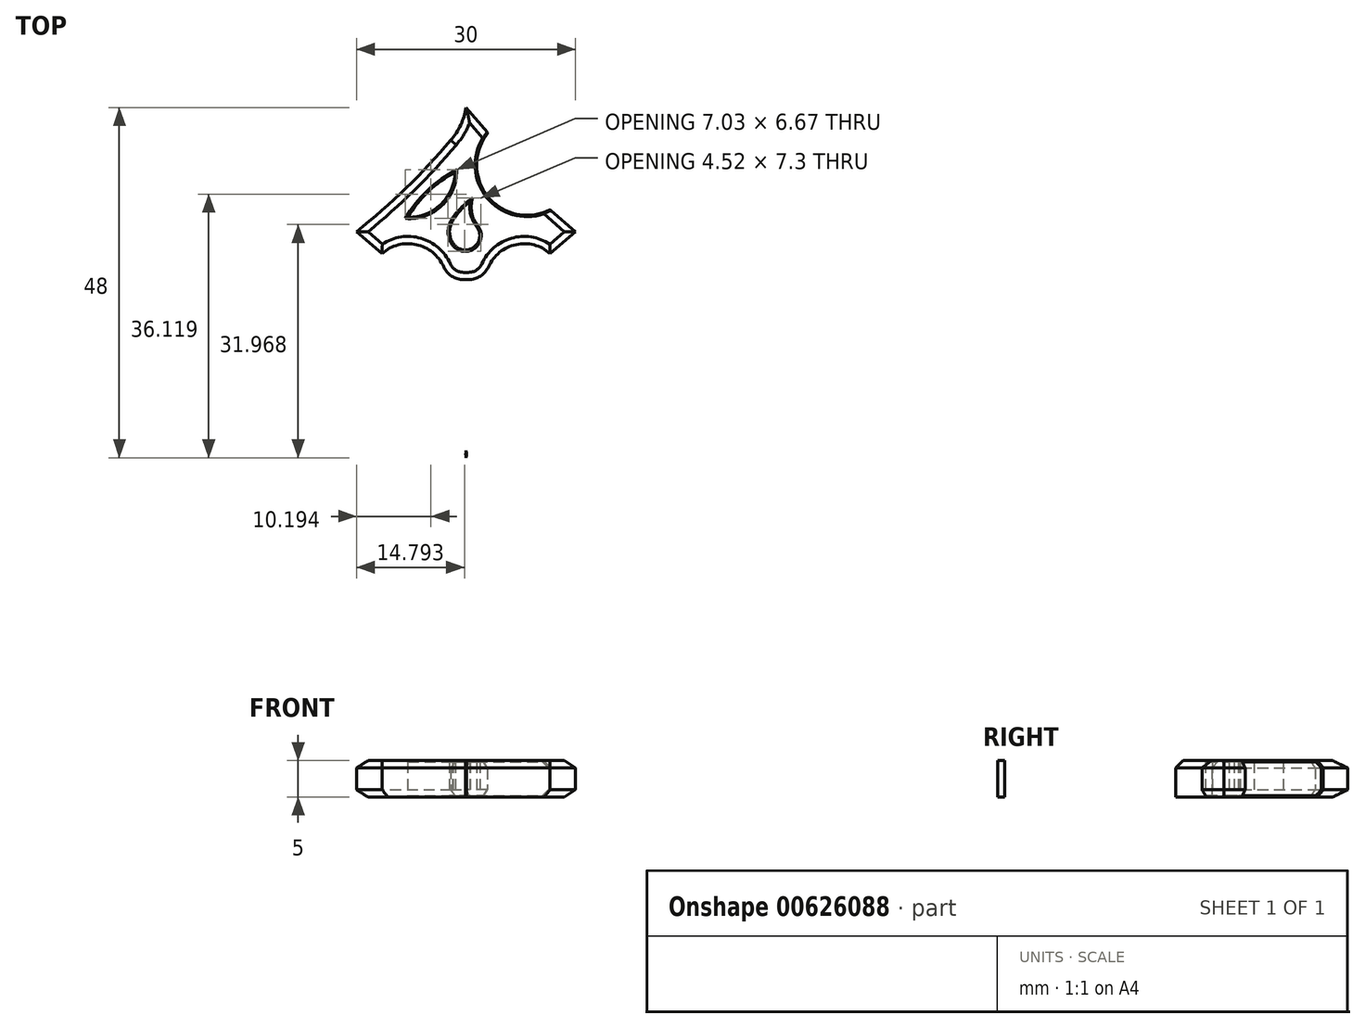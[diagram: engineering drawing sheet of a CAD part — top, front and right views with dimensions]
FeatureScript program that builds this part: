
annotation { "Feature Type Name" : "Feature", "Feature Type Description" : "" }
export const myFeature = defineFeature(function(context is Context, id is Id, definition is map)
    precondition{}
    {
        {
            var Q0;
            Q0=qCreatedBy(makeId("Top.planeOp"),FACE);
            var sketch = newSketch(context, id + "F0", { "sketchPlane" : qUnion([Q0])});
            skLineSegment(sketch, "E0", {"start": v(0, -20.9) * mm, "end": v(3, -20.9) * mm});
            skLineSegment(sketch, "E1", {"start": v(3, -20.9) * mm, "end": v(0, -20.9) * mm});
            skLineSegment(sketch, "E2", {"start": v(0, -20.9) * mm, "end": v(-3, -20.9) * mm});
            skLineSegment(sketch, "E3", {"start": v(-11.5, 6.6) * mm, "end": v(-11.5, 3.6) * mm});
            skLineSegment(sketch, "E4", {"start": v(11.5, 6.6) * mm, "end": v(11.5, 9.6) * mm});
            skLineSegment(sketch, "E5", {"start": v(11.5, 6.6) * mm, "end": v(11.5, 3.6) * mm});
            skLineSegment(sketch, "E6", {"start": v(0, 20.1) * mm, "end": v(3, 20.1) * mm});
            skLineSegment(sketch, "E7", {"start": v(0, 23.6) * mm, "end": v(3, 20.1) * mm});
            skLineSegment(sketch, "E8", {"start": v(15, 6.6) * mm, "end": v(11.5, 9.6) * mm});
            skLineSegment(sketch, "E9", {"start": v(15, 6.6) * mm, "end": v(11.5, 3.6) * mm});
            skLineSegment(sketch, "E10", {"start": v(0, -24.4) * mm, "end": v(3, -20.9) * mm});
            skLineSegment(sketch, "E11", {"start": v(0, -24.4) * mm, "end": v(-3, -20.9) * mm});
            skLineSegment(sketch, "E12", {"start": v(-11.5, 3.6) * mm, "end": v(-15, 6.6) * mm});
            skArc(sketch, "E13", {"start": v(-2.11, 19.11) * mm, "mid": v(-0.74, 21.2) * mm, "end": v(0, 23.6) * mm});
            skArc(sketch, "E14", {"start": v(-3, -20.9) * mm, "mid": v(-2.26, -10.46) * mm, "end": v(-2.62, 0) * mm});
            skArc(sketch, "E15", {"start": v(2.62, 0) * mm, "mid": v(2.26, -10.46) * mm, "end": v(3, -20.9) * mm});
            skArc(sketch, "E16", {"start": v(3, 20.1) * mm, "mid": v(2.98, 11.38) * mm, "end": v(11.5, 9.6) * mm});
            skLineSegment(sketch, "E17", {"start": v(-2.62, 0) * mm, "end": v(2.62, 0) * mm});
            skArc(sketch, "E18", {"start": v(-2.62, 0) * mm, "mid": v(-5.95, 4.54) * mm, "end": v(-11.5, 3.6) * mm});
            skArc(sketch, "E19", {"start": v(11.5, 3.6) * mm, "mid": v(5.95, 4.54) * mm, "end": v(2.62, 0) * mm});
            skArc(sketch, "E20", {"start": v(-7.98, 8.56) * mm, "mid": v(-3.46, 10.3) * mm, "end": v(-1.5, 14.72) * mm});
            skArc(sketch, "E21", {"start": v(-1.5, 14.72) * mm, "mid": v(-5.16, 12.08) * mm, "end": v(-7.98, 8.56) * mm});
            skArc(sketch, "E22", {"start": v(-15, 6.6) * mm, "mid": v(-8.24, 12.52) * mm, "end": v(-2.11, 19.11) * mm});
            skArc(sketch, "E23.0", {"start": v(-1.8, 5.01) * mm, "mid": v(1.02, 4.42) * mm, "end": v(1.45, 7.28) * mm});
            skArc(sketch, "E23.1", {"start": v(-1.88, 8.01) * mm, "mid": v(-2.27, 6.5) * mm, "end": v(-1.8, 5.01) * mm});
            skArc(sketch, "E24", {"start": v(0.58, 10.72) * mm, "mid": v(0.63, 8.9) * mm, "end": v(1.45, 7.28) * mm});
            skArc(sketch, "E25.trimOffspring", {"start": v(0.58, 10.72) * mm, "mid": v(-0.78, 9.48) * mm, "end": v(-1.88, 8.01) * mm});
            skSolve(sketch);
        }
        {
            var Q0;
            Q0=makeQuery(id+"F0.imprint","IMPRINT",FACE,{"disambiguationData":[TD([[makeQuery(id+"F0.imprint","IMPRINT",EDGE,{"derivedFrom":sQuery(id+"F0.wireOp",EDGE,"E1")}),-1.0]])]});
            var Q1;
            Q1=makeQuery(id+"F0.imprint","IMPRINT",FACE,{"disambiguationData":[TD([[makeQuery(id+"F0.imprint","IMPRINT",EDGE,{"derivedFrom":sQuery(id+"F0.wireOp",EDGE,"E1")}),1.0]])]});
            var Q2;
            Q2=makeQuery(id+"F0.imprint","IMPRINT",FACE,{"disambiguationData":[TD([[makeQuery(id+"F0.imprint","IMPRINT",EDGE,{"derivedFrom":sQuery(id+"F0.wireOp",EDGE,"E2")}),1.0]])]});
            var Q3;
            Q3=makeQuery(id+"F0.imprint","IMPRINT",FACE,{"disambiguationData":[TD([[makeQuery(id+"F0.imprint","IMPRINT",EDGE,{"derivedFrom":sQuery(id+"F0.wireOp",EDGE,"E4")}),-1.0]])]});
            var Q4;
            Q4=makeQuery(id+"F0.imprint","IMPRINT",FACE,{"disambiguationData":[TD([[makeQuery(id+"F0.imprint","IMPRINT",EDGE,{"derivedFrom":sQuery(id+"F0.wireOp",EDGE,"E4")}),1.0]])]});
            extrude(context, id + "F1", {"entities" : qUnion([Q0, Q1, Q2, Q3, Q4]), "depth" : 5 * mm, "offsetDistance" : 25 * mm});
        }
        {
            var Q0;
            Q0=makeQuery(id+"F1.opExtrude","SWEPT_EDGE",EDGE,{"disambiguationData":[OSD([sQuery(id+"F0.wireOp",EDGE,"k5tiwp8b-9EdK-JkDD-DdHM-JNxogL43b4vN"),sQuery(id+"F0.wireOp",EDGE,"E14")])]});
            var Q1;
            Q1=makeQuery(id+"F1.opExtrude","SWEPT_EDGE",EDGE,{"disambiguationData":[OSD([sQuery(id+"F0.wireOp",EDGE,"OUly3ajt-BEFw-R3yL-lqqk-aftP4KGx7Pbo"),sQuery(id+"F0.wireOp",EDGE,"E15")])]});
            var Q2;
            Q2=makeQuery(id+"F1.opExtrude","SWEPT_EDGE",EDGE,{"disambiguationData":[OSD([sQuery(id+"F0.wireOp",EDGE,"DrP2rqQ1-pYKq-EQtg-Zn2L-h3fUdfiGWgRb"),sQuery(id+"F0.wireOp",EDGE,"bePwl0fg-5cNm-J5ec-Xls5-XPhkgMzvfDfz")])]});
            fillet(context, id + "F2", {"entities" : qUnion([Q0, Q1, Q2]), "radius" : 3 * mm, "tangentPropagation" : true, "allowEdgeOverflow" : false});
        }
        {
            var Q0;
            Q0=makeQuery(id+"F1.opExtrude","CAP_EDGE",EDGE,{"disambiguationData":[OSD([sQuery(id+"F0.wireOp",EDGE,"hekDzvRY-LMJm-puWf-Dj4v-NQ24gZlVSRom")])],"isStart":false});
            var Q1;
            {var subQ0=sQuery(id+"F0.wireOp",EDGE,"hekDzvRY-LMJm-puWf-Dj4v-NQ24gZlVSRom");var subQ1=sQuery(id+"F0.wireOp",EDGE,"k5tiwp8b-9EdK-JkDD-DdHM-JNxogL43b4vN");Q1=makeQuery(id+"F2.opFillet","BLEND_EDGE",EDGE,{"blendedFrom":[makeQuery(id+"F1.opExtrude","SWEPT_EDGE",EDGE,{"disambiguationData":[OSD([subQ1,subQ0])]}),makeQuery(id+"F1.opExtrude","CAP_FACE",FACE,{"disambiguationData":[OSD([sQuery(id+"F0.wireOp",EDGE,"E7"),sQuery(id+"F0.wireOp",EDGE,"E8"),sQuery(id+"F0.wireOp",EDGE,"E9"),sQuery(id+"F0.wireOp",EDGE,"E10"),sQuery(id+"F0.wireOp",EDGE,"E11"),sQuery(id+"F0.wireOp",EDGE,"E12"),sQuery(id+"F0.wireOp",EDGE,"DrP2rqQ1-pYKq-EQtg-Zn2L-h3fUdfiGWgRb"),sQuery(id+"F0.wireOp",EDGE,"q6FidOOv-z0Xa-3gcV-Vxu2-K6z96FLS8LiD"),sQuery(id+"F0.wireOp",EDGE,"wHTpVqTk-c9Ss-kXag-DP7R-Z39pMIFVuknn"),sQuery(id+"F0.wireOp",EDGE,"bePwl0fg-5cNm-J5ec-Xls5-XPhkgMzvfDfz"),sQuery(id+"F0.wireOp",EDGE,"OUly3ajt-BEFw-R3yL-lqqk-aftP4KGx7Pbo"),subQ1,subQ0,sQuery(id+"F0.wireOp",EDGE,"mn51xUnX-rDYS-26zJ-xgYu-js4L2MmEVdlG"),sQuery(id+"F0.wireOp",EDGE,"lCkpgf7s-SHDd-Mj0l-YXK1-aCLSxgwuS06x"),sQuery(id+"F0.wireOp",EDGE,"lZJrJr9u-5WJ1-CQOP-RMIl-6jj2P56iwayc"),sQuery(id+"F0.wireOp",EDGE,"E13"),sQuery(id+"F0.wireOp",EDGE,"1a699431-0b08-407c-8c22-9d53338cef66.0"),sQuery(id+"F0.wireOp",EDGE,"1a699431-0b08-407c-8c22-9d53338cef66.1"),sQuery(id+"F0.wireOp",EDGE,"1a699431-0b08-407c-8c22-9d53338cef66.2"),sQuery(id+"F0.wireOp",EDGE,"1a699431-0b08-407c-8c22-9d53338cef66.3"),sQuery(id+"F0.wireOp",EDGE,"1a699431-0b08-407c-8c22-9d53338cef66.4"),sQuery(id+"F0.wireOp",EDGE,"1a699431-0b08-407c-8c22-9d53338cef66.5")])],"isStart":false})],"blendedInto":[makeQuery(id+"F1.opExtrude","CAP_FACE",FACE,{"disambiguationData":[OSD([sQuery(id+"F0.wireOp",EDGE,"E7"),sQuery(id+"F0.wireOp",EDGE,"E8"),sQuery(id+"F0.wireOp",EDGE,"E9"),sQuery(id+"F0.wireOp",EDGE,"E10"),sQuery(id+"F0.wireOp",EDGE,"E11"),sQuery(id+"F0.wireOp",EDGE,"E12"),sQuery(id+"F0.wireOp",EDGE,"DrP2rqQ1-pYKq-EQtg-Zn2L-h3fUdfiGWgRb"),sQuery(id+"F0.wireOp",EDGE,"q6FidOOv-z0Xa-3gcV-Vxu2-K6z96FLS8LiD"),sQuery(id+"F0.wireOp",EDGE,"wHTpVqTk-c9Ss-kXag-DP7R-Z39pMIFVuknn"),sQuery(id+"F0.wireOp",EDGE,"bePwl0fg-5cNm-J5ec-Xls5-XPhkgMzvfDfz"),sQuery(id+"F0.wireOp",EDGE,"OUly3ajt-BEFw-R3yL-lqqk-aftP4KGx7Pbo"),subQ1,subQ0,sQuery(id+"F0.wireOp",EDGE,"mn51xUnX-rDYS-26zJ-xgYu-js4L2MmEVdlG"),sQuery(id+"F0.wireOp",EDGE,"lCkpgf7s-SHDd-Mj0l-YXK1-aCLSxgwuS06x"),sQuery(id+"F0.wireOp",EDGE,"lZJrJr9u-5WJ1-CQOP-RMIl-6jj2P56iwayc"),sQuery(id+"F0.wireOp",EDGE,"E13"),sQuery(id+"F0.wireOp",EDGE,"1a699431-0b08-407c-8c22-9d53338cef66.0"),sQuery(id+"F0.wireOp",EDGE,"1a699431-0b08-407c-8c22-9d53338cef66.1"),sQuery(id+"F0.wireOp",EDGE,"1a699431-0b08-407c-8c22-9d53338cef66.2"),sQuery(id+"F0.wireOp",EDGE,"1a699431-0b08-407c-8c22-9d53338cef66.3"),sQuery(id+"F0.wireOp",EDGE,"1a699431-0b08-407c-8c22-9d53338cef66.4"),sQuery(id+"F0.wireOp",EDGE,"1a699431-0b08-407c-8c22-9d53338cef66.5")])],"isStart":false})]});}
            var Q2;
            Q2=makeQuery(id+"F1.opExtrude","CAP_EDGE",EDGE,{"disambiguationData":[OSD([sQuery(id+"F0.wireOp",EDGE,"k5tiwp8b-9EdK-JkDD-DdHM-JNxogL43b4vN")])],"isStart":false});
            var Q3;
            Q3=makeQuery(id+"F1.opExtrude","CAP_EDGE",EDGE,{"disambiguationData":[OSD([sQuery(id+"F0.wireOp",EDGE,"E12")])],"isStart":false});
            var Q4;
            Q4=makeQuery(id+"F1.opExtrude","CAP_EDGE",EDGE,{"disambiguationData":[OSD([sQuery(id+"F0.wireOp",EDGE,"lZJrJr9u-5WJ1-CQOP-RMIl-6jj2P56iwayc")])],"isStart":false});
            var Q5;
            Q5=makeQuery(id+"F1.opExtrude","CAP_EDGE",EDGE,{"disambiguationData":[OSD([sQuery(id+"F0.wireOp",EDGE,"E13")])],"isStart":false});
            var Q6;
            Q6=makeQuery(id+"F1.opExtrude","CAP_EDGE",EDGE,{"disambiguationData":[OSD([sQuery(id+"F0.wireOp",EDGE,"E7")])],"isStart":false});
            var Q7;
            Q7=makeQuery(id+"F1.opExtrude","CAP_EDGE",EDGE,{"disambiguationData":[OSD([sQuery(id+"F0.wireOp",EDGE,"DrP2rqQ1-pYKq-EQtg-Zn2L-h3fUdfiGWgRb")])],"isStart":false});
            var Q8;
            {var subQ0=sQuery(id+"F0.wireOp",EDGE,"bePwl0fg-5cNm-J5ec-Xls5-XPhkgMzvfDfz");var subQ1=sQuery(id+"F0.wireOp",EDGE,"DrP2rqQ1-pYKq-EQtg-Zn2L-h3fUdfiGWgRb");Q8=makeQuery(id+"F2.opFillet","BLEND_EDGE",EDGE,{"blendedFrom":[makeQuery(id+"F1.opExtrude","SWEPT_EDGE",EDGE,{"disambiguationData":[OSD([subQ1,subQ0])]}),makeQuery(id+"F1.opExtrude","CAP_FACE",FACE,{"disambiguationData":[OSD([sQuery(id+"F0.wireOp",EDGE,"E7"),sQuery(id+"F0.wireOp",EDGE,"E8"),sQuery(id+"F0.wireOp",EDGE,"E9"),sQuery(id+"F0.wireOp",EDGE,"E10"),sQuery(id+"F0.wireOp",EDGE,"E11"),sQuery(id+"F0.wireOp",EDGE,"E12"),subQ1,sQuery(id+"F0.wireOp",EDGE,"q6FidOOv-z0Xa-3gcV-Vxu2-K6z96FLS8LiD"),sQuery(id+"F0.wireOp",EDGE,"wHTpVqTk-c9Ss-kXag-DP7R-Z39pMIFVuknn"),subQ0,sQuery(id+"F0.wireOp",EDGE,"OUly3ajt-BEFw-R3yL-lqqk-aftP4KGx7Pbo"),sQuery(id+"F0.wireOp",EDGE,"k5tiwp8b-9EdK-JkDD-DdHM-JNxogL43b4vN"),sQuery(id+"F0.wireOp",EDGE,"hekDzvRY-LMJm-puWf-Dj4v-NQ24gZlVSRom"),sQuery(id+"F0.wireOp",EDGE,"mn51xUnX-rDYS-26zJ-xgYu-js4L2MmEVdlG"),sQuery(id+"F0.wireOp",EDGE,"lCkpgf7s-SHDd-Mj0l-YXK1-aCLSxgwuS06x"),sQuery(id+"F0.wireOp",EDGE,"lZJrJr9u-5WJ1-CQOP-RMIl-6jj2P56iwayc"),sQuery(id+"F0.wireOp",EDGE,"E13"),sQuery(id+"F0.wireOp",EDGE,"1a699431-0b08-407c-8c22-9d53338cef66.0"),sQuery(id+"F0.wireOp",EDGE,"1a699431-0b08-407c-8c22-9d53338cef66.1"),sQuery(id+"F0.wireOp",EDGE,"1a699431-0b08-407c-8c22-9d53338cef66.2"),sQuery(id+"F0.wireOp",EDGE,"1a699431-0b08-407c-8c22-9d53338cef66.3"),sQuery(id+"F0.wireOp",EDGE,"1a699431-0b08-407c-8c22-9d53338cef66.4"),sQuery(id+"F0.wireOp",EDGE,"1a699431-0b08-407c-8c22-9d53338cef66.5")])],"isStart":false})],"blendedInto":[makeQuery(id+"F1.opExtrude","CAP_FACE",FACE,{"disambiguationData":[OSD([sQuery(id+"F0.wireOp",EDGE,"E7"),sQuery(id+"F0.wireOp",EDGE,"E8"),sQuery(id+"F0.wireOp",EDGE,"E9"),sQuery(id+"F0.wireOp",EDGE,"E10"),sQuery(id+"F0.wireOp",EDGE,"E11"),sQuery(id+"F0.wireOp",EDGE,"E12"),subQ1,sQuery(id+"F0.wireOp",EDGE,"q6FidOOv-z0Xa-3gcV-Vxu2-K6z96FLS8LiD"),sQuery(id+"F0.wireOp",EDGE,"wHTpVqTk-c9Ss-kXag-DP7R-Z39pMIFVuknn"),subQ0,sQuery(id+"F0.wireOp",EDGE,"OUly3ajt-BEFw-R3yL-lqqk-aftP4KGx7Pbo"),sQuery(id+"F0.wireOp",EDGE,"k5tiwp8b-9EdK-JkDD-DdHM-JNxogL43b4vN"),sQuery(id+"F0.wireOp",EDGE,"hekDzvRY-LMJm-puWf-Dj4v-NQ24gZlVSRom"),sQuery(id+"F0.wireOp",EDGE,"mn51xUnX-rDYS-26zJ-xgYu-js4L2MmEVdlG"),sQuery(id+"F0.wireOp",EDGE,"lCkpgf7s-SHDd-Mj0l-YXK1-aCLSxgwuS06x"),sQuery(id+"F0.wireOp",EDGE,"lZJrJr9u-5WJ1-CQOP-RMIl-6jj2P56iwayc"),sQuery(id+"F0.wireOp",EDGE,"E13"),sQuery(id+"F0.wireOp",EDGE,"1a699431-0b08-407c-8c22-9d53338cef66.0"),sQuery(id+"F0.wireOp",EDGE,"1a699431-0b08-407c-8c22-9d53338cef66.1"),sQuery(id+"F0.wireOp",EDGE,"1a699431-0b08-407c-8c22-9d53338cef66.2"),sQuery(id+"F0.wireOp",EDGE,"1a699431-0b08-407c-8c22-9d53338cef66.3"),sQuery(id+"F0.wireOp",EDGE,"1a699431-0b08-407c-8c22-9d53338cef66.4"),sQuery(id+"F0.wireOp",EDGE,"1a699431-0b08-407c-8c22-9d53338cef66.5")])],"isStart":false})]});}
            var Q9;
            Q9=makeQuery(id+"F1.opExtrude","CAP_EDGE",EDGE,{"disambiguationData":[OSD([sQuery(id+"F0.wireOp",EDGE,"bePwl0fg-5cNm-J5ec-Xls5-XPhkgMzvfDfz")])],"isStart":false});
            var Q10;
            Q10=makeQuery(id+"F1.opExtrude","CAP_EDGE",EDGE,{"disambiguationData":[OSD([sQuery(id+"F0.wireOp",EDGE,"E8")])],"isStart":false});
            var Q11;
            Q11=makeQuery(id+"F1.opExtrude","CAP_EDGE",EDGE,{"disambiguationData":[OSD([sQuery(id+"F0.wireOp",EDGE,"E9")])],"isStart":false});
            var Q12;
            Q12=makeQuery(id+"F1.opExtrude","CAP_EDGE",EDGE,{"disambiguationData":[OSD([sQuery(id+"F0.wireOp",EDGE,"OUly3ajt-BEFw-R3yL-lqqk-aftP4KGx7Pbo")])],"isStart":false});
            var Q13;
            {var subQ0=sQuery(id+"F0.wireOp",EDGE,"mn51xUnX-rDYS-26zJ-xgYu-js4L2MmEVdlG");var subQ1=sQuery(id+"F0.wireOp",EDGE,"OUly3ajt-BEFw-R3yL-lqqk-aftP4KGx7Pbo");Q13=makeQuery(id+"F2.opFillet","BLEND_EDGE",EDGE,{"blendedFrom":[makeQuery(id+"F1.opExtrude","SWEPT_EDGE",EDGE,{"disambiguationData":[OSD([subQ1,subQ0])]}),makeQuery(id+"F1.opExtrude","CAP_FACE",FACE,{"disambiguationData":[OSD([sQuery(id+"F0.wireOp",EDGE,"E7"),sQuery(id+"F0.wireOp",EDGE,"E8"),sQuery(id+"F0.wireOp",EDGE,"E9"),sQuery(id+"F0.wireOp",EDGE,"E10"),sQuery(id+"F0.wireOp",EDGE,"E11"),sQuery(id+"F0.wireOp",EDGE,"E12"),sQuery(id+"F0.wireOp",EDGE,"DrP2rqQ1-pYKq-EQtg-Zn2L-h3fUdfiGWgRb"),sQuery(id+"F0.wireOp",EDGE,"q6FidOOv-z0Xa-3gcV-Vxu2-K6z96FLS8LiD"),sQuery(id+"F0.wireOp",EDGE,"wHTpVqTk-c9Ss-kXag-DP7R-Z39pMIFVuknn"),sQuery(id+"F0.wireOp",EDGE,"bePwl0fg-5cNm-J5ec-Xls5-XPhkgMzvfDfz"),subQ1,sQuery(id+"F0.wireOp",EDGE,"k5tiwp8b-9EdK-JkDD-DdHM-JNxogL43b4vN"),sQuery(id+"F0.wireOp",EDGE,"hekDzvRY-LMJm-puWf-Dj4v-NQ24gZlVSRom"),subQ0,sQuery(id+"F0.wireOp",EDGE,"lCkpgf7s-SHDd-Mj0l-YXK1-aCLSxgwuS06x"),sQuery(id+"F0.wireOp",EDGE,"lZJrJr9u-5WJ1-CQOP-RMIl-6jj2P56iwayc"),sQuery(id+"F0.wireOp",EDGE,"E13"),sQuery(id+"F0.wireOp",EDGE,"1a699431-0b08-407c-8c22-9d53338cef66.0"),sQuery(id+"F0.wireOp",EDGE,"1a699431-0b08-407c-8c22-9d53338cef66.1"),sQuery(id+"F0.wireOp",EDGE,"1a699431-0b08-407c-8c22-9d53338cef66.2"),sQuery(id+"F0.wireOp",EDGE,"1a699431-0b08-407c-8c22-9d53338cef66.3"),sQuery(id+"F0.wireOp",EDGE,"1a699431-0b08-407c-8c22-9d53338cef66.4"),sQuery(id+"F0.wireOp",EDGE,"1a699431-0b08-407c-8c22-9d53338cef66.5")])],"isStart":false})],"blendedInto":[makeQuery(id+"F1.opExtrude","CAP_FACE",FACE,{"disambiguationData":[OSD([sQuery(id+"F0.wireOp",EDGE,"E7"),sQuery(id+"F0.wireOp",EDGE,"E8"),sQuery(id+"F0.wireOp",EDGE,"E9"),sQuery(id+"F0.wireOp",EDGE,"E10"),sQuery(id+"F0.wireOp",EDGE,"E11"),sQuery(id+"F0.wireOp",EDGE,"E12"),sQuery(id+"F0.wireOp",EDGE,"DrP2rqQ1-pYKq-EQtg-Zn2L-h3fUdfiGWgRb"),sQuery(id+"F0.wireOp",EDGE,"q6FidOOv-z0Xa-3gcV-Vxu2-K6z96FLS8LiD"),sQuery(id+"F0.wireOp",EDGE,"wHTpVqTk-c9Ss-kXag-DP7R-Z39pMIFVuknn"),sQuery(id+"F0.wireOp",EDGE,"bePwl0fg-5cNm-J5ec-Xls5-XPhkgMzvfDfz"),subQ1,sQuery(id+"F0.wireOp",EDGE,"k5tiwp8b-9EdK-JkDD-DdHM-JNxogL43b4vN"),sQuery(id+"F0.wireOp",EDGE,"hekDzvRY-LMJm-puWf-Dj4v-NQ24gZlVSRom"),subQ0,sQuery(id+"F0.wireOp",EDGE,"lCkpgf7s-SHDd-Mj0l-YXK1-aCLSxgwuS06x"),sQuery(id+"F0.wireOp",EDGE,"lZJrJr9u-5WJ1-CQOP-RMIl-6jj2P56iwayc"),sQuery(id+"F0.wireOp",EDGE,"E13"),sQuery(id+"F0.wireOp",EDGE,"1a699431-0b08-407c-8c22-9d53338cef66.0"),sQuery(id+"F0.wireOp",EDGE,"1a699431-0b08-407c-8c22-9d53338cef66.1"),sQuery(id+"F0.wireOp",EDGE,"1a699431-0b08-407c-8c22-9d53338cef66.2"),sQuery(id+"F0.wireOp",EDGE,"1a699431-0b08-407c-8c22-9d53338cef66.3"),sQuery(id+"F0.wireOp",EDGE,"1a699431-0b08-407c-8c22-9d53338cef66.4"),sQuery(id+"F0.wireOp",EDGE,"1a699431-0b08-407c-8c22-9d53338cef66.5")])],"isStart":false})]});}
            var Q14;
            Q14=makeQuery(id+"F1.opExtrude","CAP_EDGE",EDGE,{"disambiguationData":[OSD([sQuery(id+"F0.wireOp",EDGE,"mn51xUnX-rDYS-26zJ-xgYu-js4L2MmEVdlG")])],"isStart":false});
            var Q15;
            Q15=makeQuery(id+"F1.opExtrude","CAP_EDGE",EDGE,{"disambiguationData":[OSD([sQuery(id+"F0.wireOp",EDGE,"k5tiwp8b-9EdK-JkDD-DdHM-JNxogL43b4vN")])],"isStart":true});
            var Q16;
            Q16=makeQuery(id+"F1.opExtrude","CAP_EDGE",EDGE,{"disambiguationData":[OSD([sQuery(id+"F0.wireOp",EDGE,"E12")])],"isStart":true});
            var Q17;
            Q17=makeQuery(id+"F1.opExtrude","CAP_EDGE",EDGE,{"disambiguationData":[OSD([sQuery(id+"F0.wireOp",EDGE,"OUly3ajt-BEFw-R3yL-lqqk-aftP4KGx7Pbo")])],"isStart":true});
            var Q18;
            Q18=makeQuery(id+"F1.opExtrude","CAP_EDGE",EDGE,{"disambiguationData":[OSD([sQuery(id+"F0.wireOp",EDGE,"bePwl0fg-5cNm-J5ec-Xls5-XPhkgMzvfDfz")])],"isStart":true});
            var Q19;
            Q19=makeQuery(id+"F1.opExtrude","CAP_EDGE",EDGE,{"disambiguationData":[OSD([sQuery(id+"F0.wireOp",EDGE,"lZJrJr9u-5WJ1-CQOP-RMIl-6jj2P56iwayc")])],"isStart":true});
            var Q20;
            {var subQ0=sQuery(id+"F0.wireOp",EDGE,"hekDzvRY-LMJm-puWf-Dj4v-NQ24gZlVSRom");var subQ1=sQuery(id+"F0.wireOp",EDGE,"k5tiwp8b-9EdK-JkDD-DdHM-JNxogL43b4vN");Q20=makeQuery(id+"F2.opFillet","BLEND_EDGE",EDGE,{"blendedFrom":[makeQuery(id+"F1.opExtrude","SWEPT_EDGE",EDGE,{"disambiguationData":[OSD([subQ1,subQ0])]}),makeQuery(id+"F1.opExtrude","CAP_FACE",FACE,{"disambiguationData":[OSD([sQuery(id+"F0.wireOp",EDGE,"E7"),sQuery(id+"F0.wireOp",EDGE,"E8"),sQuery(id+"F0.wireOp",EDGE,"E9"),sQuery(id+"F0.wireOp",EDGE,"E10"),sQuery(id+"F0.wireOp",EDGE,"E11"),sQuery(id+"F0.wireOp",EDGE,"E12"),sQuery(id+"F0.wireOp",EDGE,"DrP2rqQ1-pYKq-EQtg-Zn2L-h3fUdfiGWgRb"),sQuery(id+"F0.wireOp",EDGE,"q6FidOOv-z0Xa-3gcV-Vxu2-K6z96FLS8LiD"),sQuery(id+"F0.wireOp",EDGE,"wHTpVqTk-c9Ss-kXag-DP7R-Z39pMIFVuknn"),sQuery(id+"F0.wireOp",EDGE,"bePwl0fg-5cNm-J5ec-Xls5-XPhkgMzvfDfz"),sQuery(id+"F0.wireOp",EDGE,"OUly3ajt-BEFw-R3yL-lqqk-aftP4KGx7Pbo"),subQ1,subQ0,sQuery(id+"F0.wireOp",EDGE,"mn51xUnX-rDYS-26zJ-xgYu-js4L2MmEVdlG"),sQuery(id+"F0.wireOp",EDGE,"lCkpgf7s-SHDd-Mj0l-YXK1-aCLSxgwuS06x"),sQuery(id+"F0.wireOp",EDGE,"lZJrJr9u-5WJ1-CQOP-RMIl-6jj2P56iwayc"),sQuery(id+"F0.wireOp",EDGE,"E13"),sQuery(id+"F0.wireOp",EDGE,"1a699431-0b08-407c-8c22-9d53338cef66.0"),sQuery(id+"F0.wireOp",EDGE,"1a699431-0b08-407c-8c22-9d53338cef66.1"),sQuery(id+"F0.wireOp",EDGE,"1a699431-0b08-407c-8c22-9d53338cef66.2"),sQuery(id+"F0.wireOp",EDGE,"1a699431-0b08-407c-8c22-9d53338cef66.3"),sQuery(id+"F0.wireOp",EDGE,"1a699431-0b08-407c-8c22-9d53338cef66.4"),sQuery(id+"F0.wireOp",EDGE,"1a699431-0b08-407c-8c22-9d53338cef66.5")])],"isStart":true})],"blendedInto":[makeQuery(id+"F1.opExtrude","CAP_FACE",FACE,{"disambiguationData":[OSD([sQuery(id+"F0.wireOp",EDGE,"E7"),sQuery(id+"F0.wireOp",EDGE,"E8"),sQuery(id+"F0.wireOp",EDGE,"E9"),sQuery(id+"F0.wireOp",EDGE,"E10"),sQuery(id+"F0.wireOp",EDGE,"E11"),sQuery(id+"F0.wireOp",EDGE,"E12"),sQuery(id+"F0.wireOp",EDGE,"DrP2rqQ1-pYKq-EQtg-Zn2L-h3fUdfiGWgRb"),sQuery(id+"F0.wireOp",EDGE,"q6FidOOv-z0Xa-3gcV-Vxu2-K6z96FLS8LiD"),sQuery(id+"F0.wireOp",EDGE,"wHTpVqTk-c9Ss-kXag-DP7R-Z39pMIFVuknn"),sQuery(id+"F0.wireOp",EDGE,"bePwl0fg-5cNm-J5ec-Xls5-XPhkgMzvfDfz"),sQuery(id+"F0.wireOp",EDGE,"OUly3ajt-BEFw-R3yL-lqqk-aftP4KGx7Pbo"),subQ1,subQ0,sQuery(id+"F0.wireOp",EDGE,"mn51xUnX-rDYS-26zJ-xgYu-js4L2MmEVdlG"),sQuery(id+"F0.wireOp",EDGE,"lCkpgf7s-SHDd-Mj0l-YXK1-aCLSxgwuS06x"),sQuery(id+"F0.wireOp",EDGE,"lZJrJr9u-5WJ1-CQOP-RMIl-6jj2P56iwayc"),sQuery(id+"F0.wireOp",EDGE,"E13"),sQuery(id+"F0.wireOp",EDGE,"1a699431-0b08-407c-8c22-9d53338cef66.0"),sQuery(id+"F0.wireOp",EDGE,"1a699431-0b08-407c-8c22-9d53338cef66.1"),sQuery(id+"F0.wireOp",EDGE,"1a699431-0b08-407c-8c22-9d53338cef66.2"),sQuery(id+"F0.wireOp",EDGE,"1a699431-0b08-407c-8c22-9d53338cef66.3"),sQuery(id+"F0.wireOp",EDGE,"1a699431-0b08-407c-8c22-9d53338cef66.4"),sQuery(id+"F0.wireOp",EDGE,"1a699431-0b08-407c-8c22-9d53338cef66.5")])],"isStart":true})]});}
            var Q21;
            Q21=makeQuery(id+"F1.opExtrude","CAP_EDGE",EDGE,{"disambiguationData":[OSD([sQuery(id+"F0.wireOp",EDGE,"hekDzvRY-LMJm-puWf-Dj4v-NQ24gZlVSRom")])],"isStart":true});
            var Q22;
            Q22=makeQuery(id+"F1.opExtrude","CAP_EDGE",EDGE,{"disambiguationData":[OSD([sQuery(id+"F0.wireOp",EDGE,"E11")])],"isStart":false});
            var Q23;
            Q23=makeQuery(id+"F1.opExtrude","CAP_EDGE",EDGE,{"disambiguationData":[OSD([sQuery(id+"F0.wireOp",EDGE,"E10")])],"isStart":false});
            var Q24;
            Q24=makeQuery(id+"F1.opExtrude","CAP_EDGE",EDGE,{"disambiguationData":[OSD([sQuery(id+"F0.wireOp",EDGE,"E11")])],"isStart":true});
            var Q25;
            Q25=makeQuery(id+"F1.opExtrude","CAP_EDGE",EDGE,{"disambiguationData":[OSD([sQuery(id+"F0.wireOp",EDGE,"E10")])],"isStart":true});
            var Q26;
            Q26=makeQuery(id+"F1.opExtrude","CAP_EDGE",EDGE,{"disambiguationData":[OSD([sQuery(id+"F0.wireOp",EDGE,"mn51xUnX-rDYS-26zJ-xgYu-js4L2MmEVdlG")])],"isStart":true});
            var Q27;
            {var subQ0=sQuery(id+"F0.wireOp",EDGE,"mn51xUnX-rDYS-26zJ-xgYu-js4L2MmEVdlG");var subQ1=sQuery(id+"F0.wireOp",EDGE,"OUly3ajt-BEFw-R3yL-lqqk-aftP4KGx7Pbo");Q27=makeQuery(id+"F2.opFillet","BLEND_EDGE",EDGE,{"blendedFrom":[makeQuery(id+"F1.opExtrude","SWEPT_EDGE",EDGE,{"disambiguationData":[OSD([subQ1,subQ0])]}),makeQuery(id+"F1.opExtrude","CAP_FACE",FACE,{"disambiguationData":[OSD([sQuery(id+"F0.wireOp",EDGE,"E7"),sQuery(id+"F0.wireOp",EDGE,"E8"),sQuery(id+"F0.wireOp",EDGE,"E9"),sQuery(id+"F0.wireOp",EDGE,"E10"),sQuery(id+"F0.wireOp",EDGE,"E11"),sQuery(id+"F0.wireOp",EDGE,"E12"),sQuery(id+"F0.wireOp",EDGE,"DrP2rqQ1-pYKq-EQtg-Zn2L-h3fUdfiGWgRb"),sQuery(id+"F0.wireOp",EDGE,"q6FidOOv-z0Xa-3gcV-Vxu2-K6z96FLS8LiD"),sQuery(id+"F0.wireOp",EDGE,"wHTpVqTk-c9Ss-kXag-DP7R-Z39pMIFVuknn"),sQuery(id+"F0.wireOp",EDGE,"bePwl0fg-5cNm-J5ec-Xls5-XPhkgMzvfDfz"),subQ1,sQuery(id+"F0.wireOp",EDGE,"k5tiwp8b-9EdK-JkDD-DdHM-JNxogL43b4vN"),sQuery(id+"F0.wireOp",EDGE,"hekDzvRY-LMJm-puWf-Dj4v-NQ24gZlVSRom"),subQ0,sQuery(id+"F0.wireOp",EDGE,"lCkpgf7s-SHDd-Mj0l-YXK1-aCLSxgwuS06x"),sQuery(id+"F0.wireOp",EDGE,"lZJrJr9u-5WJ1-CQOP-RMIl-6jj2P56iwayc"),sQuery(id+"F0.wireOp",EDGE,"E13"),sQuery(id+"F0.wireOp",EDGE,"1a699431-0b08-407c-8c22-9d53338cef66.0"),sQuery(id+"F0.wireOp",EDGE,"1a699431-0b08-407c-8c22-9d53338cef66.1"),sQuery(id+"F0.wireOp",EDGE,"1a699431-0b08-407c-8c22-9d53338cef66.2"),sQuery(id+"F0.wireOp",EDGE,"1a699431-0b08-407c-8c22-9d53338cef66.3"),sQuery(id+"F0.wireOp",EDGE,"1a699431-0b08-407c-8c22-9d53338cef66.4"),sQuery(id+"F0.wireOp",EDGE,"1a699431-0b08-407c-8c22-9d53338cef66.5")])],"isStart":true})],"blendedInto":[makeQuery(id+"F1.opExtrude","CAP_FACE",FACE,{"disambiguationData":[OSD([sQuery(id+"F0.wireOp",EDGE,"E7"),sQuery(id+"F0.wireOp",EDGE,"E8"),sQuery(id+"F0.wireOp",EDGE,"E9"),sQuery(id+"F0.wireOp",EDGE,"E10"),sQuery(id+"F0.wireOp",EDGE,"E11"),sQuery(id+"F0.wireOp",EDGE,"E12"),sQuery(id+"F0.wireOp",EDGE,"DrP2rqQ1-pYKq-EQtg-Zn2L-h3fUdfiGWgRb"),sQuery(id+"F0.wireOp",EDGE,"q6FidOOv-z0Xa-3gcV-Vxu2-K6z96FLS8LiD"),sQuery(id+"F0.wireOp",EDGE,"wHTpVqTk-c9Ss-kXag-DP7R-Z39pMIFVuknn"),sQuery(id+"F0.wireOp",EDGE,"bePwl0fg-5cNm-J5ec-Xls5-XPhkgMzvfDfz"),subQ1,sQuery(id+"F0.wireOp",EDGE,"k5tiwp8b-9EdK-JkDD-DdHM-JNxogL43b4vN"),sQuery(id+"F0.wireOp",EDGE,"hekDzvRY-LMJm-puWf-Dj4v-NQ24gZlVSRom"),subQ0,sQuery(id+"F0.wireOp",EDGE,"lCkpgf7s-SHDd-Mj0l-YXK1-aCLSxgwuS06x"),sQuery(id+"F0.wireOp",EDGE,"lZJrJr9u-5WJ1-CQOP-RMIl-6jj2P56iwayc"),sQuery(id+"F0.wireOp",EDGE,"E13"),sQuery(id+"F0.wireOp",EDGE,"1a699431-0b08-407c-8c22-9d53338cef66.0"),sQuery(id+"F0.wireOp",EDGE,"1a699431-0b08-407c-8c22-9d53338cef66.1"),sQuery(id+"F0.wireOp",EDGE,"1a699431-0b08-407c-8c22-9d53338cef66.2"),sQuery(id+"F0.wireOp",EDGE,"1a699431-0b08-407c-8c22-9d53338cef66.3"),sQuery(id+"F0.wireOp",EDGE,"1a699431-0b08-407c-8c22-9d53338cef66.4"),sQuery(id+"F0.wireOp",EDGE,"1a699431-0b08-407c-8c22-9d53338cef66.5")])],"isStart":true})]});}
            var Q28;
            Q28=makeQuery(id+"F1.opExtrude","CAP_EDGE",EDGE,{"disambiguationData":[OSD([sQuery(id+"F0.wireOp",EDGE,"E9")])],"isStart":true});
            var Q29;
            Q29=makeQuery(id+"F1.opExtrude","CAP_EDGE",EDGE,{"disambiguationData":[OSD([sQuery(id+"F0.wireOp",EDGE,"E8")])],"isStart":true});
            var Q30;
            Q30=makeQuery(id+"F1.opExtrude","CAP_EDGE",EDGE,{"disambiguationData":[OSD([sQuery(id+"F0.wireOp",EDGE,"E7")])],"isStart":true});
            var Q31;
            Q31=makeQuery(id+"F1.opExtrude","CAP_EDGE",EDGE,{"disambiguationData":[OSD([sQuery(id+"F0.wireOp",EDGE,"DrP2rqQ1-pYKq-EQtg-Zn2L-h3fUdfiGWgRb")])],"isStart":true});
            var Q32;
            {var subQ0=sQuery(id+"F0.wireOp",EDGE,"bePwl0fg-5cNm-J5ec-Xls5-XPhkgMzvfDfz");var subQ1=sQuery(id+"F0.wireOp",EDGE,"DrP2rqQ1-pYKq-EQtg-Zn2L-h3fUdfiGWgRb");Q32=makeQuery(id+"F2.opFillet","BLEND_EDGE",EDGE,{"blendedFrom":[makeQuery(id+"F1.opExtrude","SWEPT_EDGE",EDGE,{"disambiguationData":[OSD([subQ1,subQ0])]}),makeQuery(id+"F1.opExtrude","CAP_FACE",FACE,{"disambiguationData":[OSD([sQuery(id+"F0.wireOp",EDGE,"E7"),sQuery(id+"F0.wireOp",EDGE,"E8"),sQuery(id+"F0.wireOp",EDGE,"E9"),sQuery(id+"F0.wireOp",EDGE,"E10"),sQuery(id+"F0.wireOp",EDGE,"E11"),sQuery(id+"F0.wireOp",EDGE,"E12"),subQ1,sQuery(id+"F0.wireOp",EDGE,"q6FidOOv-z0Xa-3gcV-Vxu2-K6z96FLS8LiD"),sQuery(id+"F0.wireOp",EDGE,"wHTpVqTk-c9Ss-kXag-DP7R-Z39pMIFVuknn"),subQ0,sQuery(id+"F0.wireOp",EDGE,"OUly3ajt-BEFw-R3yL-lqqk-aftP4KGx7Pbo"),sQuery(id+"F0.wireOp",EDGE,"k5tiwp8b-9EdK-JkDD-DdHM-JNxogL43b4vN"),sQuery(id+"F0.wireOp",EDGE,"hekDzvRY-LMJm-puWf-Dj4v-NQ24gZlVSRom"),sQuery(id+"F0.wireOp",EDGE,"mn51xUnX-rDYS-26zJ-xgYu-js4L2MmEVdlG"),sQuery(id+"F0.wireOp",EDGE,"lCkpgf7s-SHDd-Mj0l-YXK1-aCLSxgwuS06x"),sQuery(id+"F0.wireOp",EDGE,"lZJrJr9u-5WJ1-CQOP-RMIl-6jj2P56iwayc"),sQuery(id+"F0.wireOp",EDGE,"E13"),sQuery(id+"F0.wireOp",EDGE,"1a699431-0b08-407c-8c22-9d53338cef66.0"),sQuery(id+"F0.wireOp",EDGE,"1a699431-0b08-407c-8c22-9d53338cef66.1"),sQuery(id+"F0.wireOp",EDGE,"1a699431-0b08-407c-8c22-9d53338cef66.2"),sQuery(id+"F0.wireOp",EDGE,"1a699431-0b08-407c-8c22-9d53338cef66.3"),sQuery(id+"F0.wireOp",EDGE,"1a699431-0b08-407c-8c22-9d53338cef66.4"),sQuery(id+"F0.wireOp",EDGE,"1a699431-0b08-407c-8c22-9d53338cef66.5")])],"isStart":true})],"blendedInto":[makeQuery(id+"F1.opExtrude","CAP_FACE",FACE,{"disambiguationData":[OSD([sQuery(id+"F0.wireOp",EDGE,"E7"),sQuery(id+"F0.wireOp",EDGE,"E8"),sQuery(id+"F0.wireOp",EDGE,"E9"),sQuery(id+"F0.wireOp",EDGE,"E10"),sQuery(id+"F0.wireOp",EDGE,"E11"),sQuery(id+"F0.wireOp",EDGE,"E12"),subQ1,sQuery(id+"F0.wireOp",EDGE,"q6FidOOv-z0Xa-3gcV-Vxu2-K6z96FLS8LiD"),sQuery(id+"F0.wireOp",EDGE,"wHTpVqTk-c9Ss-kXag-DP7R-Z39pMIFVuknn"),subQ0,sQuery(id+"F0.wireOp",EDGE,"OUly3ajt-BEFw-R3yL-lqqk-aftP4KGx7Pbo"),sQuery(id+"F0.wireOp",EDGE,"k5tiwp8b-9EdK-JkDD-DdHM-JNxogL43b4vN"),sQuery(id+"F0.wireOp",EDGE,"hekDzvRY-LMJm-puWf-Dj4v-NQ24gZlVSRom"),sQuery(id+"F0.wireOp",EDGE,"mn51xUnX-rDYS-26zJ-xgYu-js4L2MmEVdlG"),sQuery(id+"F0.wireOp",EDGE,"lCkpgf7s-SHDd-Mj0l-YXK1-aCLSxgwuS06x"),sQuery(id+"F0.wireOp",EDGE,"lZJrJr9u-5WJ1-CQOP-RMIl-6jj2P56iwayc"),sQuery(id+"F0.wireOp",EDGE,"E13"),sQuery(id+"F0.wireOp",EDGE,"1a699431-0b08-407c-8c22-9d53338cef66.0"),sQuery(id+"F0.wireOp",EDGE,"1a699431-0b08-407c-8c22-9d53338cef66.1"),sQuery(id+"F0.wireOp",EDGE,"1a699431-0b08-407c-8c22-9d53338cef66.2"),sQuery(id+"F0.wireOp",EDGE,"1a699431-0b08-407c-8c22-9d53338cef66.3"),sQuery(id+"F0.wireOp",EDGE,"1a699431-0b08-407c-8c22-9d53338cef66.4"),sQuery(id+"F0.wireOp",EDGE,"1a699431-0b08-407c-8c22-9d53338cef66.5")])],"isStart":true})]});}
            var Q33;
            Q33=makeQuery(id+"F1.opExtrude","CAP_EDGE",EDGE,{"disambiguationData":[OSD([sQuery(id+"F0.wireOp",EDGE,"E13")])],"isStart":true});
            var Q34;
            Q34=makeQuery(id+"F1.opExtrude","CAP_EDGE",EDGE,{"disambiguationData":[OSD([sQuery(id+"F0.wireOp",EDGE,"E22")])],"isStart":false});
            var Q35;
            Q35=makeQuery(id+"F1.opExtrude","CAP_EDGE",EDGE,{"disambiguationData":[OSD([sQuery(id+"F0.wireOp",EDGE,"E22")])],"isStart":true});
            var Q36;
            Q36=makeQuery(id+"F1.opExtrude","CAP_EDGE",EDGE,{"disambiguationData":[OSD([sQuery(id+"F0.wireOp",EDGE,"E18")])],"isStart":false});
            var Q37;
            Q37=makeQuery(id+"F1.opExtrude","CAP_EDGE",EDGE,{"disambiguationData":[OSD([sQuery(id+"F0.wireOp",EDGE,"E14")])],"isStart":false});
            chamfer(context, id + "F3", {"entities" : qUnion([Q0, Q1, Q2, Q3, Q4, Q5, Q6, Q7, Q8, Q9, Q10, Q11, Q12, Q13, Q14, Q15, Q16, Q17, Q18, Q19, Q20, Q21, Q22, Q23, Q24, Q25, Q26, Q27, Q28, Q29, Q30, Q31, Q32, Q33, Q34, Q35, Q36, Q37]), "width" : 1 * mm, "tangentPropagation" : true});
        }
        {
            var Q0;
            Q0=makeQuery(id+"F1.opExtrude","CAP_EDGE",EDGE,{"disambiguationData":[OSD([sQuery(id+"F0.wireOp",EDGE,"0a70a7e9-7a16-4d6b-9ec8-a9e118f4038e.3")])],"isStart":true});
            var Q1;
            Q1=makeQuery(id+"F1.opExtrude","CAP_EDGE",EDGE,{"disambiguationData":[OSD([sQuery(id+"F0.wireOp",EDGE,"0a70a7e9-7a16-4d6b-9ec8-a9e118f4038e.2")])],"isStart":true});
            var Q2;
            Q2=makeQuery(id+"F1.opExtrude","CAP_EDGE",EDGE,{"disambiguationData":[OSD([sQuery(id+"F0.wireOp",EDGE,"0a70a7e9-7a16-4d6b-9ec8-a9e118f4038e.1")])],"isStart":true});
            var Q3;
            Q3=makeQuery(id+"F1.opExtrude","CAP_EDGE",EDGE,{"disambiguationData":[OSD([sQuery(id+"F0.wireOp",EDGE,"0a70a7e9-7a16-4d6b-9ec8-a9e118f4038e.4")])],"isStart":true});
            var Q4;
            Q4=makeQuery(id+"F1.opExtrude","CAP_EDGE",EDGE,{"disambiguationData":[OSD([sQuery(id+"F0.wireOp",EDGE,"0a70a7e9-7a16-4d6b-9ec8-a9e118f4038e.5")])],"isStart":true});
            var Q5;
            Q5=makeQuery(id+"F1.opExtrude","CAP_EDGE",EDGE,{"disambiguationData":[OSD([sQuery(id+"F0.wireOp",EDGE,"0a70a7e9-7a16-4d6b-9ec8-a9e118f4038e.5")])],"isStart":false});
            var Q6;
            Q6=makeQuery(id+"F1.opExtrude","CAP_EDGE",EDGE,{"disambiguationData":[OSD([sQuery(id+"F0.wireOp",EDGE,"0a70a7e9-7a16-4d6b-9ec8-a9e118f4038e.0")])],"isStart":true});
            var Q7;
            Q7=makeQuery(id+"F1.opExtrude","CAP_EDGE",EDGE,{"disambiguationData":[OSD([sQuery(id+"F0.wireOp",EDGE,"0a70a7e9-7a16-4d6b-9ec8-a9e118f4038e.4")])],"isStart":false});
            var Q8;
            Q8=makeQuery(id+"F1.opExtrude","CAP_EDGE",EDGE,{"disambiguationData":[OSD([sQuery(id+"F0.wireOp",EDGE,"0a70a7e9-7a16-4d6b-9ec8-a9e118f4038e.0")])],"isStart":false});
            var Q9;
            Q9=makeQuery(id+"F1.opExtrude","CAP_EDGE",EDGE,{"disambiguationData":[OSD([sQuery(id+"F0.wireOp",EDGE,"0a70a7e9-7a16-4d6b-9ec8-a9e118f4038e.1")])],"isStart":false});
            var Q10;
            Q10=makeQuery(id+"F1.opExtrude","CAP_EDGE",EDGE,{"disambiguationData":[OSD([sQuery(id+"F0.wireOp",EDGE,"0a70a7e9-7a16-4d6b-9ec8-a9e118f4038e.2")])],"isStart":false});
            var Q11;
            Q11=makeQuery(id+"F1.opExtrude","CAP_EDGE",EDGE,{"disambiguationData":[OSD([sQuery(id+"F0.wireOp",EDGE,"0a70a7e9-7a16-4d6b-9ec8-a9e118f4038e.3")])],"isStart":false});
            var Q12;
            Q12=makeQuery(id+"F1.opExtrude","SWEPT_FACE",FACE,{"disambiguationData":[OSD([sQuery(id+"F0.wireOp",EDGE,"E16")])]});
            var Q13;
            Q13=makeQuery(id+"F1.opExtrude","CAP_EDGE",EDGE,{"disambiguationData":[OSD([sQuery(id+"F0.wireOp",EDGE,"E20")])],"isStart":false});
            var Q14;
            Q14=makeQuery(id+"F1.opExtrude","CAP_EDGE",EDGE,{"disambiguationData":[OSD([sQuery(id+"F0.wireOp",EDGE,"E21")])],"isStart":false});
            var Q15;
            Q15=makeQuery(id+"F1.opExtrude","CAP_EDGE",EDGE,{"disambiguationData":[OSD([sQuery(id+"F0.wireOp",EDGE,"E20")])],"isStart":true});
            var Q16;
            Q16=makeQuery(id+"F1.opExtrude","CAP_EDGE",EDGE,{"disambiguationData":[OSD([sQuery(id+"F0.wireOp",EDGE,"E21")])],"isStart":true});
            var Q17;
            Q17=makeQuery(id+"F1.opExtrude","CAP_EDGE",EDGE,{"disambiguationData":[OSD([sQuery(id+"F0.wireOp",EDGE,"E25.trimOffspring")])],"isStart":false});
            var Q18;
            Q18=makeQuery(id+"F1.opExtrude","CAP_EDGE",EDGE,{"disambiguationData":[OSD([sQuery(id+"F0.wireOp",EDGE,"E24")])],"isStart":false});
            var Q19;
            Q19=makeQuery(id+"F1.opExtrude","CAP_EDGE",EDGE,{"disambiguationData":[OSD([sQuery(id+"F0.wireOp",EDGE,"E24")])],"isStart":true});
            var Q20;
            Q20=makeQuery(id+"F1.opExtrude","CAP_EDGE",EDGE,{"disambiguationData":[OSD([sQuery(id+"F0.wireOp",EDGE,"E25.trimOffspring")])],"isStart":true});
            chamfer(context, id + "F4", {"entities" : qUnion([Q0, Q1, Q2, Q3, Q4, Q5, Q6, Q7, Q8, Q9, Q10, Q11, Q12, Q13, Q14, Q15, Q16, Q17, Q18, Q19, Q20]), "width" : .2 * mm, "tangentPropagation" : true});
        }
    });
